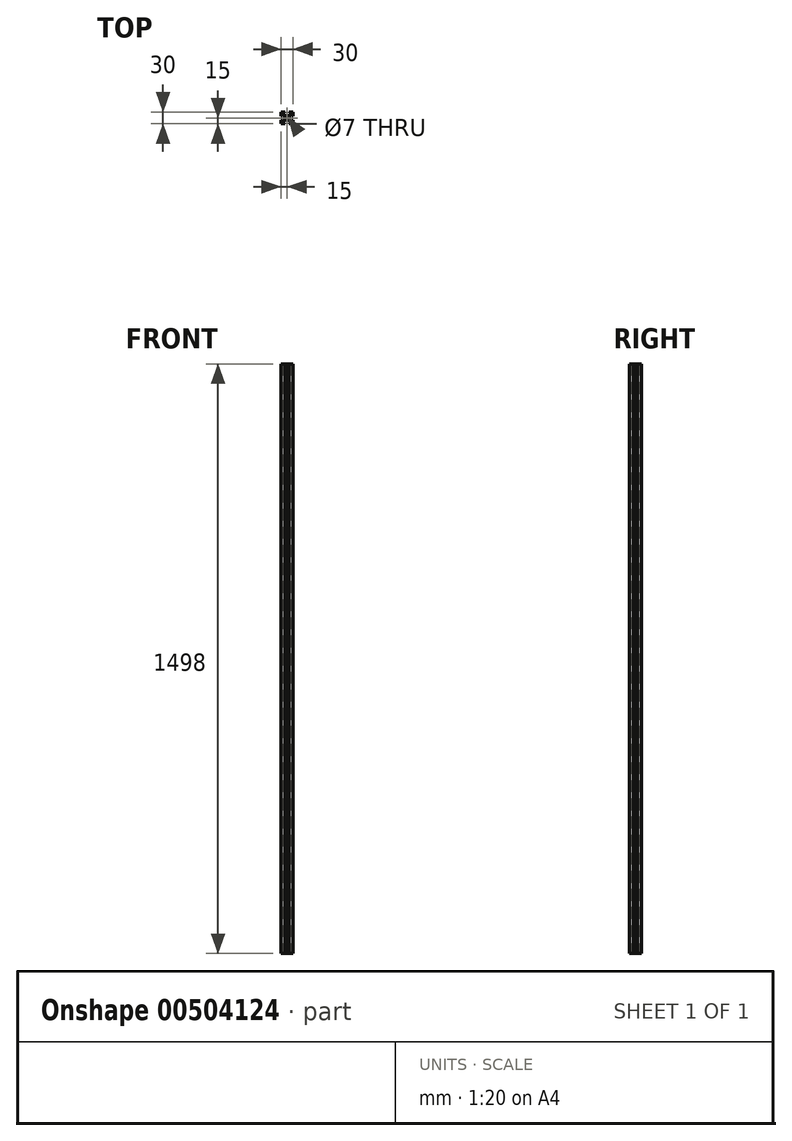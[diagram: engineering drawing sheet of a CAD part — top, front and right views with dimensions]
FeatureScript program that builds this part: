
annotation { "Feature Type Name" : "Feature", "Feature Type Description" : "" }
export const myFeature = defineFeature(function(context is Context, id is Id, definition is map)
    precondition{}
    {
        {
            var Q0;
            Q0=qCreatedBy(makeId("Top.planeOp"),FACE);
            var sketch = newSketch(context, id + "F0", { "sketchPlane" : qUnion([Q0])});
            skCircle(sketch, "E0", {"center": v(0, 0) * mm, "radius": 3.5 * mm});
            skLineSegment(sketch, "E1.bottom", {"start": v(-4.59, 6) * mm, "end": v(4.59, 6) * mm});
            skLineSegment(sketch, "E1.top", {"start": v(-4.59, -6) * mm, "end": v(4.59, -6) * mm});
            skLineSegment(sketch, "E1.left", {"start": v(-6, 4.59) * mm, "end": v(-6, -4.59) * mm});
            skLineSegment(sketch, "E1.right", {"start": v(6, 4.59) * mm, "end": v(6, -4.59) * mm});
            skLineSegment(sketch, "E2", {"start": v(-6, 4.59) * mm, "end": v(-11.41, 10) * mm});
            skLineSegment(sketch, "E3", {"start": v(-4.59, 6) * mm, "end": v(-10, 11.41) * mm});
            skLineSegment(sketch, "E4", {"start": v(-11.41, 10) * mm, "end": v(-13, 10) * mm});
            skLineSegment(sketch, "E5", {"start": v(-13, 10) * mm, "end": v(-13, 5) * mm});
            skLineSegment(sketch, "E6", {"start": v(-13, 5) * mm, "end": v(-15, 5) * mm});
            skLineSegment(sketch, "E7", {"start": v(-15, 5) * mm, "end": v(-15, 15) * mm});
            skLineSegment(sketch, "E8", {"start": v(-15, 15) * mm, "end": v(-5, 15) * mm});
            skLineSegment(sketch, "E9", {"start": v(-5, 15) * mm, "end": v(-5, 13) * mm});
            skLineSegment(sketch, "E10", {"start": v(-5, 13) * mm, "end": v(-10, 13) * mm});
            skLineSegment(sketch, "E11", {"start": v(-10, 13) * mm, "end": v(-10, 11.41) * mm});
            skPoint(sketch, "E12.orphan", {"position": v(-6, 6) * mm});
            skLineSegment(sketch, "E13", {"start": v(0, 0) * mm, "end": v(-5.3, 5.3) * mm, "construction": true});
            skLineSegment(sketch, "E14", {"start": v(-5.3, 5.3) * mm, "end": v(-6, 4.59) * mm, "construction": true});
            skLineSegment(sketch, "E15", {"start": v(-5.3, 5.3) * mm, "end": v(-4.59, 6) * mm, "construction": true});
            skLineSegment(sketch, "E16.2.0", {"start": v(15, 15) * mm, "end": v(15, 5) * mm});
            skLineSegment(sketch, "E16.2.1", {"start": v(5, 15) * mm, "end": v(15, 15) * mm});
            skLineSegment(sketch, "E16.2.2", {"start": v(5, 13) * mm, "end": v(5, 15) * mm});
            skLineSegment(sketch, "E16.2.3", {"start": v(10, 13) * mm, "end": v(5, 13) * mm});
            skLineSegment(sketch, "E16.2.4", {"start": v(10, 11.41) * mm, "end": v(10, 13) * mm});
            skLineSegment(sketch, "E16.2.5", {"start": v(4.59, 6) * mm, "end": v(10, 11.41) * mm});
            skLineSegment(sketch, "E16.2.6", {"start": v(6, 4.59) * mm, "end": v(11.41, 10) * mm});
            skLineSegment(sketch, "E16.2.7", {"start": v(13, 10) * mm, "end": v(11.41, 10) * mm});
            skLineSegment(sketch, "E16.2.8", {"start": v(13, 5) * mm, "end": v(13, 10) * mm});
            skLineSegment(sketch, "E16.2.9", {"start": v(15, 5) * mm, "end": v(13, 5) * mm});
            skLineSegment(sketch, "E16.anchor1", {"start": v(0, 0) * mm, "end": v(-15, 15) * mm, "construction": true});
            skLineSegment(sketch, "E16.anchor2", {"start": v(0, 0) * mm, "end": v(15, 15) * mm, "construction": true});
            skPoint(sketch, "E17.orphan", {"position": v(6, 6) * mm});
            skLineSegment(sketch, "E18.MirrorCS", {"start": v(-13, -5) * mm, "end": v(-15, -5) * mm});
            skLineSegment(sketch, "E19.MirrorCS", {"start": v(-15, -5) * mm, "end": v(-15, -15) * mm});
            skLineSegment(sketch, "E20.MirrorCS", {"start": v(-13, -10) * mm, "end": v(-13, -5) * mm});
            skLineSegment(sketch, "E21.MirrorCS", {"start": v(-11.41, -10) * mm, "end": v(-13, -10) * mm});
            skLineSegment(sketch, "E22.MirrorCS", {"start": v(-6, -4.59) * mm, "end": v(-11.41, -10) * mm});
            skLineSegment(sketch, "E23.MirrorCS", {"start": v(-4.59, -6) * mm, "end": v(-10, -11.41) * mm});
            skLineSegment(sketch, "E24.MirrorCS", {"start": v(-5, -13) * mm, "end": v(-10, -13) * mm});
            skLineSegment(sketch, "E25.MirrorCS", {"start": v(-10, -13) * mm, "end": v(-10, -11.41) * mm});
            skLineSegment(sketch, "E26.MirrorCS", {"start": v(-5, -15) * mm, "end": v(-5, -13) * mm});
            skLineSegment(sketch, "E27.MirrorCS", {"start": v(-15, -15) * mm, "end": v(-5, -15) * mm});
            skLineSegment(sketch, "E28.MirrorCS", {"start": v(5, -13) * mm, "end": v(5, -15) * mm});
            skLineSegment(sketch, "E29.MirrorCS", {"start": v(5, -15) * mm, "end": v(15, -15) * mm});
            skLineSegment(sketch, "E30.MirrorCS", {"start": v(15, -15) * mm, "end": v(15, -5) * mm});
            skLineSegment(sketch, "E31.MirrorCS", {"start": v(15, -5) * mm, "end": v(13, -5) * mm});
            skLineSegment(sketch, "E32.MirrorCS", {"start": v(13, -5) * mm, "end": v(13, -10) * mm});
            skLineSegment(sketch, "E33.MirrorCS", {"start": v(13, -10) * mm, "end": v(11.41, -10) * mm});
            skLineSegment(sketch, "E34.MirrorCS", {"start": v(6, -4.59) * mm, "end": v(11.41, -10) * mm});
            skLineSegment(sketch, "E35.MirrorCS", {"start": v(4.59, -6) * mm, "end": v(10, -11.41) * mm});
            skLineSegment(sketch, "E36.MirrorCS", {"start": v(10, -13) * mm, "end": v(5, -13) * mm});
            skLineSegment(sketch, "E37.MirrorCS", {"start": v(10, -11.41) * mm, "end": v(10, -13) * mm});
            skPoint(sketch, "E38.orphan", {"position": v(-6, -6) * mm});
            skPoint(sketch, "E39.orphan", {"position": v(6, -6) * mm});
            skSolve(sketch);
        }
        {
            var Q0;
            Q0=qSketchRegion(id+"F0",true);
            extrude(context, id + "F1", {"entities" : qUnion([Q0]), "depth" : 1498 * mm});
        }
    });
